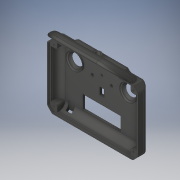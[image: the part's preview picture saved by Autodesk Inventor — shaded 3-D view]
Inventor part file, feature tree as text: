
AUTODESK INVENTOR PART (.ipt)
format: ipt  version: 2019.4 (Build 234330000, 330)  size: 1,756,672 bytes
history: native  units: in
note: dims shown in document units (in); Inventor stores cm internally (conversion verified against a paired STEP export)
features: sketch x16, move_body x13, extrude x12, fillet x11, direct_edit x7, imported_body x1
ambient origin geometry x8: Origin, YZ Plane, XZ Plane, XY Plane, X Axis, Y Axis, Z Axis, Center Point
bodies: Solid1 (feature_tree)
feature tree (60):
  imported_body  "Base1"
  fillet  "Fillet1"  Radius=0.4724in
  fillet  "Fillet2"  Radius=0.1969in
  fillet  "Fillet3"  Radius=0.1969in
  direct_edit  "Direct Edit1"
  extrude  "Extrusion1"  Depth=0.0787in TaperAngle=0.0deg
  fillet  "Fillet4"  Radius=0.1575in
  extrude  "Extrusion3"  Depth=0.3937in
  extrude  "Extrusion4"  Depth=0.2362in
  sketch  "Sketch5"  dims[d12=-0.0394in d13=0.0in d14=0.0in d16=0.1575in d17=0.0in]
  sketch  "Sketch6"  dims[d18=0.3937in d25=0.0079in]
  extrude  "Extrusion5"  Depth=0.0157in
  extrude  "Extrusion6"  Depth=0.0079in
  extrude  "Extrusion7"  Depth=0.0157in
  extrude  "Extrusion8"  TaperAngle=90.0deg  [1 undecoded]
  sketch  "Sketch11"  dims[d34=0.0079in d35=90.0deg d36=0.2362in d37=0.0157in d38=0.0157in d39=0.0157in d40=0.0157in d41=0.0157in]
  fillet  "Fillet6"  Radius=0.2362in
  fillet  "Fillet7"  Radius=0.0157in
  fillet  "Fillet8"  Radius=0.0157in
  fillet  "Fillet9"  Radius=0.0157in
  fillet  "Fillet10"  Radius=0.0157in
  fillet  "Fillet11"  Radius=0.0157in
  direct_edit  "Direct Edit2"
  direct_edit  "Direct Edit3"
  extrude  "Extrusion10"  Depth=0.0157in
  direct_edit  "Direct Edit4"
  sketch  "Sketch14"  dims[d44=0.0157in d45=0.0157in d46=0.0in]
  extrude  "Extrusion11"  Depth=0.0157in TaperAngle=0.0deg
  sketch  "Sketch16"  dims[d49=0.2362in d50=0.0157in]
  extrude  "Extrusion12"  Depth=0.0157in
  direct_edit  "Direct Edit5"
  direct_edit  "Direct Edit6"
  direct_edit  "Direct Edit7"
  extrude  "Extrusion13"  Depth=0.0157in
  extrude  "Extrusion14"  Depth=0.0079in
  fillet  "Fillet12"  [1 undecoded]
  sketch  "Sketch1"  dims[d3=0.0in d4=0.0787in d5=0.0in d6=0.0in d7=0.0394in d8=0.0in]
  sketch  "Sketch3"  dims[d9=0.0394in d10=0.0in d11=0.0in]
  sketch  "Sketch7"  dims[d26=0.0157in d27=0.2362in]
  sketch  "Sketch8"  dims[d28=0.0079in d29=0.0157in]
  sketch  "Sketch9"  dims[d30=0.2362in d31=0.0079in]
  sketch  "Sketch10"  dims[d32=0.2362in d33=0.0157in]
  sketch  "Sketch13"  dims[d42=0.0157in d43=0.0157in]
  sketch  "Sketch15"  dims[d47=0.0079in d48=0.0157in]
  sketch  "Sketch17"  dims[d51=0.0157in d52=0.0079in d53=90.0deg]
  sketch  "Sketch18"  dims[d54=0.2362in]
  sketch  "Sketch19"  dims[d55=0.0157in d56=0.0157in d57=0.0157in d58=0.0079in d59=90.0deg d60=0.2362in d61=0.0157in d62=0.0157in d63=0.0157in d64=0.0079in d65=0.0in d66=0.0157in d67=0.2362in d68=0.0157in d69=0.0157in d70=0.0in d71=1.5748in d72=0.0in d73=1.9685in d75=1.9685in d76=45.0deg d77=0.7818in d78=0.0in d79=0.7818in d80=0.0in d81=0.3937in d82=4.252in d83=0.0in d84=1.0236in d85=1.378in d86=0.3937in d87=0.3937in d88=0.1181in d89=0.0787in d102=0.0787in d103=0.0in d104=0.0in d105=-0.0394in d106=0.0in d107=0.0in d108=0.315in d109=0.1575in d110=0.5512in d111=0.0in d113=0.0in d114=0.0in d115=-0.0394in d116=0.1181in d117=0.1181in d118=0.1181in d119=0.1181in d120=0.5512in d121=0.0in d122=-0.0787in d123=0.0in d124=0.0in d125=0.0in d126=360.0deg d127=0.1575in d128=0.0in d129=0.0in d130=0.1575in d131=0.0394in d132=0.0in d133=0.0in d134=0.0787in d135=0.0039in d136=2.8031in d137=1.0157in d138=0.3937in d139=0.0in d140=0.0in d141=0.0in d142=-0.0079in d143=0.0in d144=0.0in d145=-0.0059in d146=0.0in d147=0.0in d148=-0.0059in d149=0.8858in d150=0.4724in d151=0.4331in d152=0.2756in d153=0.7874in d154=0.0in d155=1.2598in d156=1.2598in d157=0.1181in d158=0.0in d159=0.0787in]
  move_body  "Move1"
  move_body  "Move2"
  move_body  "Move3"
  move_body  "Move4"
  move_body  "Move5"
  move_body  "Move6"
  move_body  "Move7"
  move_body  "Move8"
  move_body  "Move9"
  move_body  "Move10"
  move_body  "Move11"
  move_body  "Move12"
  move_body  "Move13"
note: 2 required parameter values undecoded (feature->parameter linkage not recoverable at this tier; creation-order binding heuristic only, values carry confidence <= 0.55)
